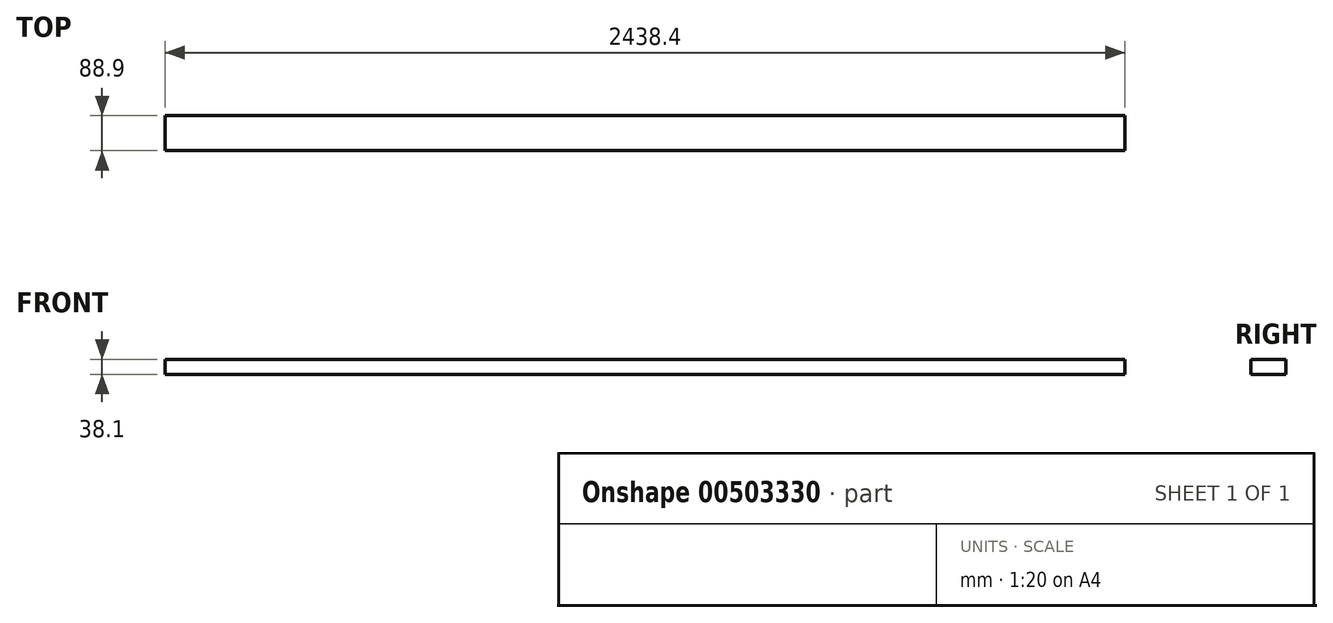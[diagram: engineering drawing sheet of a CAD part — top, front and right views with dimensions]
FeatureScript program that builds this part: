
annotation { "Feature Type Name" : "Feature", "Feature Type Description" : "" }
export const myFeature = defineFeature(function(context is Context, id is Id, definition is map)
    precondition{}
    {
        {
            var Q0;
            Q0=qCreatedBy(makeId("Front.planeOp"),FACE);
            var sketch = newSketch(context, id + "F0", { "sketchPlane" : qUnion([Q0])});
            skLineSegment(sketch, "E0.bottom", {"start": v(-1208.7, -73.6) * mm, "end": v(1229.7, -73.6) * mm});
            skLineSegment(sketch, "E0.top", {"start": v(-1208.7, -111.7) * mm, "end": v(1229.7, -111.7) * mm});
            skLineSegment(sketch, "E0.left", {"start": v(-1208.7, -73.6) * mm, "end": v(-1208.7, -111.7) * mm});
            skLineSegment(sketch, "E0.right", {"start": v(1229.7, -73.6) * mm, "end": v(1229.7, -111.7) * mm});
            skSolve(sketch);
        }
        {
            var Q0;
            Q0 = qSketchRegion(id + "F0", true);
            var Q1;
            Q1=sQuery(id+"F0.wireOp",EDGE,"E0.bottom");
            extrude(context, id + "F1", {"entities" : qUnion([Q0]), "surfaceEntities" : qUnion([Q1]), "endBound" : BoundingType.SYMMETRIC, "depth" : 88.9 * mm});
        }
    });
